# Revit family: GAZ SOL
name_source: partatom
category: Leuchten
revit_build: Autodesk Revit 2018 (Build: 20190510_1515(x64)
units: mm (PartAtom-declared; Revit-internal decimal feet)

## family parameters
Arbeitsebenenbasiert = Nein
Beim Laden mit Abzugskörper schneiden = Ja
Bemaßung runder Anschluss = Durchmesser verwenden
Gemeinsam genutzt = Nein
Immer vertikal = Ja
Lichtquelle = Ja
OmniClass-Nummer = 23.80.70.11.21
OmniClass-Titel = Emergency Lighting
Raumberechnungspunkt = Nein
Teiletyp = Normal

## types (4) — shared parameters
Ausbildung Leuchtmittel = LED
B_Montage DA Seil = Nein
B_Montage DE = Nein
B_Montage DE Seil = Nein
B_Montage WE = Nein
Bauelement = Sicherheitsleuchte
Bauteil, Not-/Sicherheitsbeleuchtung = Sicherheitsleuchte
Bemessungsbetriebsdauer h Notlichtstrahler = -
Bemessungsbetriebsspannung V = 230 AC/220 DC (+/- 20%)
Beschreibung = universell einsetzbare Allgemeinleuchte, wahlweise mit integrierter Sicherheitsbeleuchtung
Betriebsart Notbeleuchtung = Bereitschaftsschaltung
Farbfilter = 16777215
Farbtemperaturverschiebung bei Dämpfen der Lampe = <Keine Auswahl>
Gehäusefarbe = weiß
Größe des Lichtquellensymbols = 20 mm  [stored 0.0656168 ft]
Hersteller = GAZ Notstromsysteme GmbH
Lampe = LED
Leuchte Bauweise = im Kompaktgehäuse
Produktinformationen = https://gaz.de
Schutzklasse elektrische Betriebsmittel = I
Spannung = 230 V
URL = https://gaz.de
Umgebungstemperatur Grad C = -10 bis +40
Werkstoff, Gehäuse Notbeleuchtung = Stahl, beschichtet
_Versorgung = 1
zero-valued in all types: B_Einfüge Versatz von oben, B_MK Versatz hinten, B_MK Versatz links, B_MK Versatz oben, B_MK Versatz rechts

## per-type parameters (varying)
- SOL S R DA: B_Anschluss Versatz hinten=190 mm; B_Anschuss Versatz oben=10 mm  [stored 0.0328084 ft]; B_Bel Versatz hinten=190 mm; B_Bel Versatz oben=225 mm  [stored 0.738189 ft]; B_Einfüge Versatz von vorn=190 mm; B_Halter Dicke=16 mm  [stored 0.0524934 ft]; B_Halter Durchmesser=330 mm; B_Leuchtkörper Bogen=220 mm  [stored 0.721785 ft]; B_Leuchtkörper Höhe=109 mm  [stored 0.357612 ft]; B_Leuchtkörper Radius=190 mm; B_MK Form rund Decke=Ja; B_MK Form rund Wand=Nein; B_MK Versatz unten=109 mm  [stored 0.357612 ft]; B_MK Versatz vorn=0 mm  [stored 0 ft]; B_Montage=1; B_Montage DA=Ja; B_Montage WA=Nein; B_Sol Typ=1; Breite=380 mm; Durchmesser=380 mm; Höhe=125 mm  [stored 0.410105 ft]; Montage Notleuchte=Deckenanbau; Scheinlast=17 VA; Schutzart=IP40; Tiefe=380 mm; Typenkommentare=Deckenanbau
- SOL M R DA: B_Anschluss Versatz hinten=245 mm  [stored 0.803806 ft]; B_Anschuss Versatz oben=10 mm  [stored 0.0328084 ft]; B_Bel Versatz hinten=245 mm  [stored 0.803806 ft]; B_Bel Versatz oben=260 mm  [stored 0.853018 ft]; B_Einfüge Versatz von vorn=245 mm  [stored 0.803806 ft]; B_Halter Dicke=26 mm; B_Halter Durchmesser=435 mm  [stored 1.42717 ft]; B_Leuchtkörper Bogen=290 mm  [stored 0.951444 ft]; B_Leuchtkörper Höhe=134 mm  [stored 0.439633 ft]; B_Leuchtkörper Radius=245 mm  [stored 0.803806 ft]; B_MK Form rund Decke=Ja; B_MK Form rund Wand=Nein; B_MK Versatz unten=134 mm  [stored 0.439633 ft]; B_MK Versatz vorn=0 mm  [stored 0 ft]; B_Montage=1; B_Montage DA=Ja; B_Montage WA=Nein; B_Sol Typ=2; Breite=490 mm  [stored 1.60761 ft]; Durchmesser=490 mm  [stored 1.60761 ft]; Höhe=160 mm  [stored 0.524934 ft]; Montage Notleuchte=Deckenanbau; Scheinlast=32 VA; Schutzart=wählbar: IP40, IP65; Tiefe=490 mm  [stored 1.60761 ft]; Typenkommentare=Deckenanbau
- SOL S R WA: B_Anschluss Versatz hinten=115 mm  [stored 0.377297 ft]; B_Anschuss Versatz oben=190 mm; B_Bel Versatz hinten=225 mm  [stored 0.738189 ft]; B_Bel Versatz oben=190 mm; B_Einfüge Versatz von vorn=125 mm  [stored 0.410105 ft]; B_Halter Dicke=16 mm  [stored 0.0524934 ft]; B_Halter Durchmesser=330 mm; B_Leuchtkörper Bogen=220 mm  [stored 0.721785 ft]; B_Leuchtkörper Höhe=109 mm  [stored 0.357612 ft]; B_Leuchtkörper Radius=190 mm; B_MK Form rund Decke=Nein; B_MK Form rund Wand=Ja; B_MK Versatz unten=0 mm  [stored 0 ft]; B_MK Versatz vorn=109 mm  [stored 0.357612 ft]; B_Montage=5; B_Montage DA=Nein; B_Montage WA=Ja; B_Sol Typ=1; Breite=380 mm; Durchmesser=380 mm; Höhe=380 mm; Montage Notleuchte=Wandanbau; Scheinlast=17 VA; Schutzart=IP40; Tiefe=125 mm  [stored 0.410105 ft]; Typenkommentare=Wandanbau
- SOL M R WA: B_Anschluss Versatz hinten=150 mm; B_Anschuss Versatz oben=245 mm  [stored 0.803806 ft]; B_Bel Versatz hinten=260 mm  [stored 0.853018 ft]; B_Bel Versatz oben=245 mm  [stored 0.803806 ft]; B_Einfüge Versatz von vorn=160 mm  [stored 0.524934 ft]; B_Halter Dicke=26 mm; B_Halter Durchmesser=435 mm  [stored 1.42717 ft]; B_Leuchtkörper Bogen=290 mm  [stored 0.951444 ft]; B_Leuchtkörper Höhe=134 mm  [stored 0.439633 ft]; B_Leuchtkörper Radius=245 mm  [stored 0.803806 ft]; B_MK Form rund Decke=Nein; B_MK Form rund Wand=Ja; B_MK Versatz unten=0 mm  [stored 0 ft]; B_MK Versatz vorn=134 mm  [stored 0.439633 ft]; B_Montage=5; B_Montage DA=Nein; B_Montage WA=Ja; B_Sol Typ=2; Breite=490 mm  [stored 1.60761 ft]; Durchmesser=490 mm  [stored 1.60761 ft]; Höhe=490 mm  [stored 1.60761 ft]; Montage Notleuchte=Wandanbau; Scheinlast=32 VA; Schutzart=wählbar: IP40, IP65; Tiefe=160 mm  [stored 0.524934 ft]; Typenkommentare=Wandanbau

note: column(s) folded — value = type name in every type: Modell

note: [stored X ft] marks values corroborated as IEEE doubles in the binary element streams (Revit-internal decimal feet)
